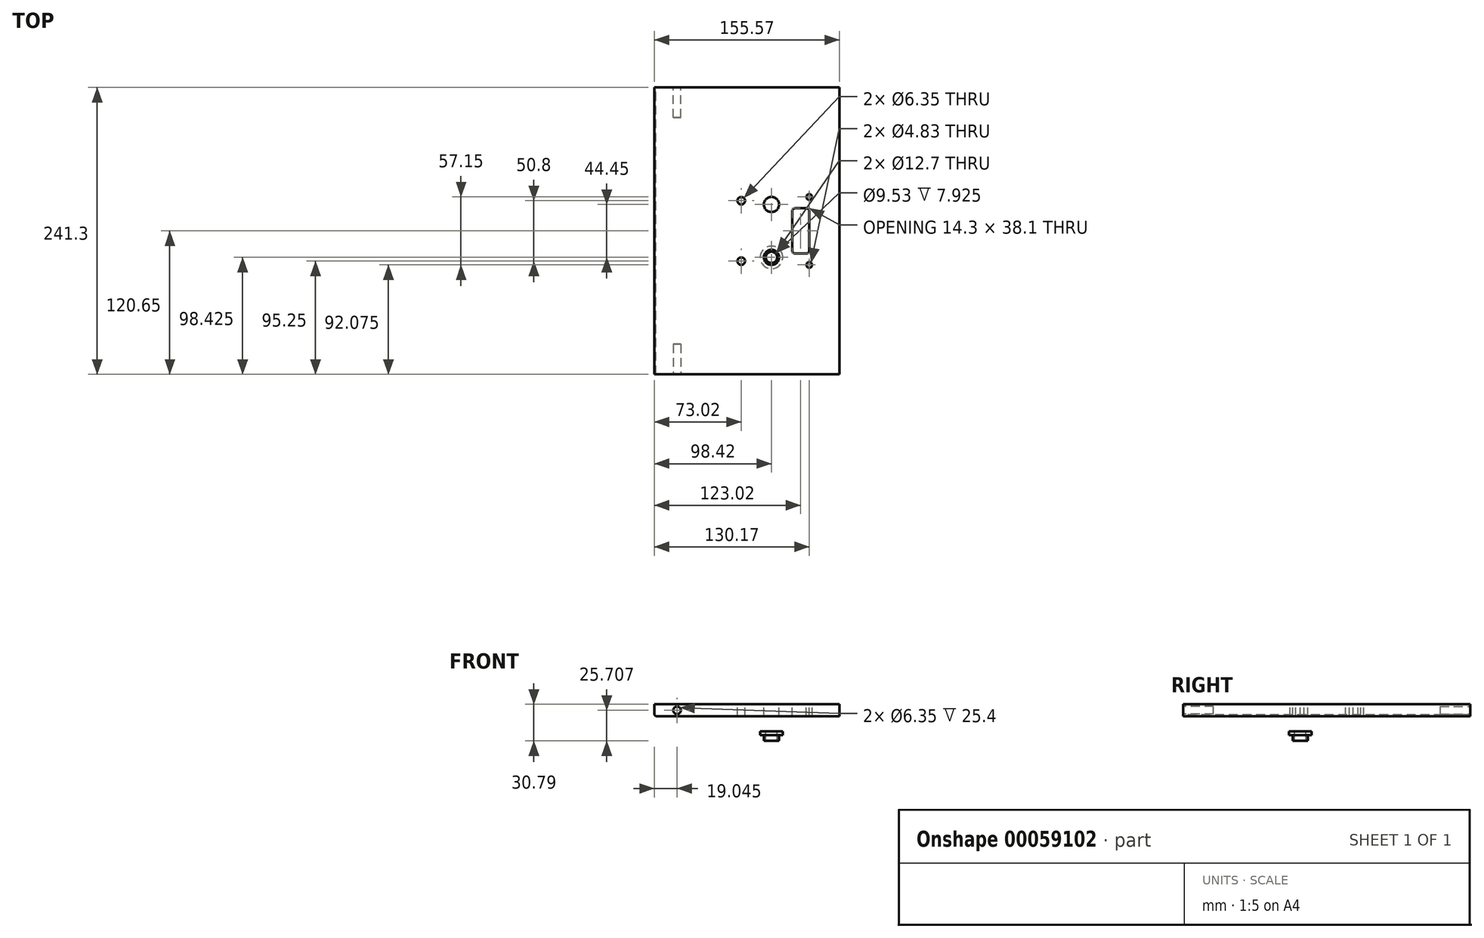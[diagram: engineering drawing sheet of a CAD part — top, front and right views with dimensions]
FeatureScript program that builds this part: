
annotation { "Feature Type Name" : "Feature", "Feature Type Description" : "" }
export const myFeature = defineFeature(function(context is Context, id is Id, definition is map)
    precondition{}
    {
        {
            var Q0;
            Q0=qCreatedBy(makeId("Front.planeOp"),FACE);
            var sketch = newSketch(context, id + "F0", { "sketchPlane" : qUnion([Q0])});
            skLineSegment(sketch, "E0.rect.bottom", {"start": v(50.8, -4.76) * mm, "end": v(-88.9, -4.76) * mm});
            skLineSegment(sketch, "E0.rect.top", {"start": v(50.8, 5.4) * mm, "end": v(-88.9, 5.4) * mm});
            skLineSegment(sketch, "E0.rect.right", {"start": v(-88.9, -4.76) * mm, "end": v(-88.9, 5.4) * mm});
            skPoint(sketch, "E0.rect.middle", {"position": v(0, 0) * mm});
            skLineSegment(sketch, "E1", {"start": v(50.8, 5.4) * mm, "end": v(50.8, -4.76) * mm});
            skSolve(sketch);
        }
        {
            var Q0;
            Q0=makeQuery(id+"F0.imprint","IMPRINT",FACE,{"disambiguationData":[TD([[makeQuery(id+"F0.imprint","IMPRINT",EDGE,{"derivedFrom":sQuery(id+"F0.wireOp",EDGE,"E0.rect.bottom")}),-1.0]])]});
            extrude(context, id + "F1", {"entities" : qUnion([Q0]), "depth" : 120.65 * mm, "hasSecondDirection" : true, "secondDirectionOppositeDirection" : true, "secondDirectionDepth" : 120.65 * mm});
        }
        {
            var Q0;
            Q0=makeQuery(id+"F1.opExtrude","SWEPT_FACE",FACE,{"disambiguationData":[OSD([sQuery(id+"F0.wireOp",EDGE,"E0.rect.top")])]});
            var sketch = newSketch(context, id + "F2", { "sketchPlane" : qUnion([Q0])});
            skLineSegment(sketch, "E2", {"start": v(-19.05, 120.65) * mm, "end": v(-19.05, -120.65) * mm, "construction": true});
            skLineSegment(sketch, "E3", {"start": v(-31.75, 120.65) * mm, "end": v(-31.75, -120.65) * mm, "construction": true});
            skLineSegment(sketch, "E4", {"start": v(-88.9, 25.4) * mm, "end": v(50.8, 25.4) * mm, "construction": true});
            skLineSegment(sketch, "E5", {"start": v(-88.9, -25.4) * mm, "end": v(50.8, -25.4) * mm, "construction": true});
            skCircle(sketch, "E6", {"center": v(-31.75, 25.4) * mm, "radius": 3.18 * mm});
            skCircle(sketch, "E7", {"center": v(-31.75, -25.4) * mm, "radius": 3.18 * mm});
            skLineSegment(sketch, "E8", {"start": v(-6.35, 120.65) * mm, "end": v(-6.35, -120.65) * mm, "construction": true});
            skCircle(sketch, "E9", {"center": v(-6.35, 22.22) * mm, "radius": 6.35 * mm});
            skCircle(sketch, "E10", {"center": v(-6.35, -22.23) * mm, "radius": 6.35 * mm});
            skLineSegment(sketch, "E11", {"start": v(9.52, 120.65) * mm, "end": v(9.53, -120.65) * mm, "construction": true});
            skLineSegment(sketch, "E12", {"start": v(25.4, 120.65) * mm, "end": v(25.4, -120.65) * mm, "construction": true});
            skPoint(sketch, "E13.oppositeSnap0", {"position": v(25.4, 0) * mm});
            skLineSegment(sketch, "E13.left", {"start": v(11.1, 19.05) * mm, "end": v(11.1, -19.05) * mm});
            skLineSegment(sketch, "E13.right", {"start": v(25.4, 19.05) * mm, "end": v(25.4, -19.05) * mm});
            skLineSegment(sketch, "E14", {"start": v(11.1, 19.05) * mm, "end": v(25.4, 19.05) * mm});
            skLineSegment(sketch, "E15", {"start": v(11.1, -19.05) * mm, "end": v(25.4, -19.05) * mm});
            skPoint(sketch, "E16.orphan", {"position": v(25.4, -25.4) * mm});
            skLineSegment(sketch, "E17", {"start": v(9.52, 28.58) * mm, "end": v(25.4, 28.58) * mm, "construction": true});
            skLineSegment(sketch, "E18", {"start": v(9.52, -28.57) * mm, "end": v(25.4, -28.57) * mm, "construction": true});
            skCircle(sketch, "E19", {"center": v(25.4, 28.58) * mm, "radius": 2.41 * mm});
            skCircle(sketch, "E20", {"center": v(25.4, -28.57) * mm, "radius": 2.41 * mm});
            skLineSegment(sketch, "E21", {"start": v(-88.9, 0) * mm, "end": v(50.8, 0) * mm, "construction": true});
            skSolve(sketch);
        }
        {
            var Q0;
            Q0=makeQuery(id+"F2.imprint","IMPRINT",FACE,{"disambiguationData":[TD([[makeQuery(id+"F2.imprint","IMPRINT",EDGE,{"derivedFrom":sQuery(id+"F2.wireOp",EDGE,"E6")}),1.0]])]});
            var Q1;
            Q1=makeQuery(id+"F2.imprint","IMPRINT",FACE,{"disambiguationData":[TD([[makeQuery(id+"F2.imprint","IMPRINT",EDGE,{"derivedFrom":sQuery(id+"F2.wireOp",EDGE,"E7")}),1.0]])]});
            var Q2;
            Q2=makeQuery(id+"F2.imprint","IMPRINT",FACE,{"disambiguationData":[TD([[makeQuery(id+"F2.imprint","IMPRINT",EDGE,{"derivedFrom":sQuery(id+"F2.wireOp",EDGE,"E9")}),1.0]])]});
            var Q3;
            Q3=makeQuery(id+"F2.imprint","IMPRINT",FACE,{"disambiguationData":[TD([[makeQuery(id+"F2.imprint","IMPRINT",EDGE,{"derivedFrom":sQuery(id+"F2.wireOp",EDGE,"E10")}),1.0]])]});
            var Q4;
            Q4=makeQuery(id+"F2.imprint","IMPRINT",FACE,{"disambiguationData":[TD([[makeQuery(id+"F2.imprint","IMPRINT",EDGE,{"derivedFrom":sQuery(id+"F2.wireOp",EDGE,"E19")}),1.0]])]});
            var Q5;
            Q5=makeQuery(id+"F2.imprint","IMPRINT",FACE,{"disambiguationData":[TD([[makeQuery(id+"F2.imprint","IMPRINT",EDGE,{"derivedFrom":sQuery(id+"F2.wireOp",EDGE,"E20")}),1.0]])]});
            var Q6;
            Q6=makeQuery(id+"F2.imprint","IMPRINT",FACE,{"disambiguationData":[TD([[makeQuery(id+"F2.imprint","IMPRINT",EDGE,{"derivedFrom":sQuery(id+"F2.wireOp",EDGE,"E13.left")}),1.0]])]});
            extrude(context, id + "F3", {"entities" : qUnion([Q0, Q1, Q2, Q3, Q4, Q5, Q6]), "operationType" : NewBodyOperationType.REMOVE, "endBound" : BoundingType.THROUGH_ALL, "oppositeDirection" : true, "depth" : 25.4 * mm});
        }
        {
            var Q0;
            Q0=makeQuery(id+"F3.boolean.opBoolean","COPY",EDGE,{"derivedFrom":makeQuery(id+"F3.opExtrude","SWEPT_EDGE",EDGE,{"disambiguationData":[OSD([sQuery(id+"F2.wireOp",EDGE,"E13.left"),sQuery(id+"F2.wireOp",EDGE,"E14")])]})});
            var Q1;
            Q1=makeQuery(id+"F3.boolean.opBoolean","COPY",EDGE,{"derivedFrom":makeQuery(id+"F3.opExtrude","SWEPT_EDGE",EDGE,{"disambiguationData":[OSD([sQuery(id+"F2.wireOp",EDGE,"E13.right"),sQuery(id+"F2.wireOp",EDGE,"E14")])]})});
            var Q2;
            Q2=makeQuery(id+"F3.boolean.opBoolean","COPY",EDGE,{"derivedFrom":makeQuery(id+"F3.opExtrude","SWEPT_EDGE",EDGE,{"disambiguationData":[OSD([sQuery(id+"F2.wireOp",EDGE,"E13.left"),sQuery(id+"F2.wireOp",EDGE,"E15")])]})});
            var Q3;
            Q3=makeQuery(id+"F3.boolean.opBoolean","COPY",EDGE,{"derivedFrom":makeQuery(id+"F3.opExtrude","SWEPT_EDGE",EDGE,{"disambiguationData":[OSD([sQuery(id+"F2.wireOp",EDGE,"E13.right"),sQuery(id+"F2.wireOp",EDGE,"E15")])]})});
            fillet(context, id + "F4", {"entities" : qUnion([Q0, Q1, Q2, Q3]), "radius" : 2.54 * mm, "tangentPropagation" : true, "allowEdgeOverflow" : false});
        }
        {
            var Q0;
            Q0=makeQuery(id+"F1.opExtrude","SWEPT_FACE",FACE,{"disambiguationData":[OSD([sQuery(id+"F0.wireOp",EDGE,"E0.rect.right")])]});
            extrude(context, id + "F5", {"entities" : qUnion([Q0]), "operationType" : NewBodyOperationType.ADD, "depth" : 15.88 * mm});
        }
        {
            var Q0;
            {var subQ0=sQuery(id+"F0.wireOp",EDGE,"E0.rect.right");Q0=makeQuery(id+"F5.boolean.opBoolean","MERGE",FACE,{"derivedFrom":[makeQuery(id+"F1.opExtrude","CAP_FACE",FACE,{"disambiguationData":[OSD([sQuery(id+"F0.wireOp",EDGE,"E0.rect.bottom"),sQuery(id+"F0.wireOp",EDGE,"E0.rect.top"),subQ0,sQuery(id+"F0.wireOp",EDGE,"E1")])],"isStart":false}),makeQuery(id+"F5.opExtrude","SWEPT_FACE",FACE,{"disambiguationData":[OSD([subQ0]),TDD([makeQuery(id+"F1.opExtrude","CAP_EDGE",EDGE,{"disambiguationData":[OSD([subQ0])],"isStart":false})])]})]});}
            var sketch = newSketch(context, id + "F6", { "sketchPlane" : qUnion([Q0])});
            skLineSegment(sketch, "E22", {"start": v(-58.45, 0) * mm, "end": v(-104.77, 0) * mm, "construction": true});
            skLineSegment(sketch, "E23", {"start": v(-85.72, 5.4) * mm, "end": v(-85.72, -4.76) * mm, "construction": true});
            skCircle(sketch, "E24", {"center": v(-85.72, 0.32) * mm, "radius": 3.18 * mm});
            skSolve(sketch);
        }
        {
            var Q0;
            Q0=makeQuery(id+"F6.imprint","IMPRINT",FACE,{"disambiguationData":[TD([[makeQuery(id+"F6.imprint","IMPRINT",EDGE,{"derivedFrom":sQuery(id+"F6.wireOp",EDGE,"E24")}),1.0]])]});
            extrude(context, id + "F7", {"entities" : qUnion([Q0]), "operationType" : NewBodyOperationType.REMOVE, "oppositeDirection" : true, "depth" : 25.4 * mm});
        }
        {
            var Q0;
            {var subQ0=sQuery(id+"F0.wireOp",EDGE,"E0.rect.right");Q0=makeQuery(id+"F5.boolean.opBoolean","MERGE",FACE,{"derivedFrom":[makeQuery(id+"F1.opExtrude","CAP_FACE",FACE,{"disambiguationData":[OSD([sQuery(id+"F0.wireOp",EDGE,"E0.rect.bottom"),sQuery(id+"F0.wireOp",EDGE,"E0.rect.top"),subQ0,sQuery(id+"F0.wireOp",EDGE,"E1")])],"isStart":true}),makeQuery(id+"F5.opExtrude","SWEPT_FACE",FACE,{"disambiguationData":[OSD([subQ0]),TDD([makeQuery(id+"F1.opExtrude","CAP_EDGE",EDGE,{"disambiguationData":[OSD([subQ0])],"isStart":true})])]})]});}
            var sketch = newSketch(context, id + "F8", { "sketchPlane" : qUnion([Q0])});
            skLineSegment(sketch, "E25", {"start": v(63.13, 0) * mm, "end": v(104.77, 0) * mm, "construction": true});
            skLineSegment(sketch, "E26", {"start": v(85.72, 5.4) * mm, "end": v(85.72, -4.76) * mm, "construction": true});
            skCircle(sketch, "E27", {"center": v(85.72, 0.32) * mm, "radius": 3.18 * mm});
            skSolve(sketch);
        }
        {
            var Q0;
            Q0=makeQuery(id+"F8.imprint","IMPRINT",FACE,{"disambiguationData":[TD([[makeQuery(id+"F8.imprint","IMPRINT",EDGE,{"derivedFrom":sQuery(id+"F8.wireOp",EDGE,"E27")}),1.0]])]});
            extrude(context, id + "F9", {"entities" : qUnion([Q0]), "operationType" : NewBodyOperationType.REMOVE, "oppositeDirection" : true, "depth" : 25.4 * mm});
        }
        {
            var Q0;
            Q0=makeQuery(id+"F5.opExtrude","CAP_EDGE",EDGE,{"disambiguationData":[OSD([sQuery(id+"F0.wireOp",EDGE,"E0.rect.bottom"),sQuery(id+"F0.wireOp",EDGE,"E0.rect.right")])],"isStart":false});
            chamfer(context, id + "F10", {"entities" : qUnion([Q0]), "width" : 1.27 * mm, "tangentPropagation" : true});
        }
        {
            var Q0;
            {var subQ0=sQuery(id+"F0.wireOp",EDGE,"E0.rect.bottom");Q0=makeQuery(id+"F5.boolean.opBoolean","MERGE",FACE,{"derivedFrom":[makeQuery(id+"F1.opExtrude","SWEPT_FACE",FACE,{"disambiguationData":[OSD([subQ0])]}),makeQuery(id+"F5.opExtrude","SWEPT_FACE",FACE,{"disambiguationData":[OSD([subQ0,sQuery(id+"F0.wireOp",EDGE,"E0.rect.right")])]})]});}
            cPlane(context, id + "F11", {"entities" : qUnion([Q0]), "cplaneType" : CPlaneType.OFFSET, "offset" : 12.7 * mm, "width" : 152.4 * mm, "height" : 152.4 * mm});
        }
        {
            var Q0;
            Q0=qCreatedBy(id+"F11.planeOp",FACE);
            var sketch = newSketch(context, id + "F12", { "sketchPlane" : qUnion([Q0])});
            skCircle(sketch, "E28.0", {"center": v(-6.35, 22.23) * mm, "radius": 6.35 * mm, "construction": true});
            skCircle(sketch, "E29", {"center": v(-6.35, 22.23) * mm, "radius": 9.53 * mm});
            skCircle(sketch, "E30", {"center": v(-6.35, 22.23) * mm, "radius": 4.76 * mm});
            skSolve(sketch);
        }
        {
            var Q0;
            Q0=makeQuery(id+"F12.imprint","IMPRINT",FACE,{"disambiguationData":[TD([[makeQuery(id+"F12.imprint","IMPRINT",EDGE,{"derivedFrom":sQuery(id+"F12.wireOp",EDGE,"E29")}),1.0]])]});
            extrude(context, id + "F13", {"entities" : qUnion([Q0]), "depth" : 3.17 * mm});
        }
        {
            var Q0;
            Q0=makeQuery(id+"F13.opExtrude","CAP_FACE",FACE,{"disambiguationData":[OSD([sQuery(id+"F12.wireOp",EDGE,"E29"),sQuery(id+"F12.wireOp",EDGE,"E30")])],"isStart":false});
            var sketch = newSketch(context, id + "F14", { "sketchPlane" : qUnion([Q0])});
            skCircle(sketch, "E31.0", {"center": v(-6.35, 22.23) * mm, "radius": 4.76 * mm});
            skCircle(sketch, "E32.0", {"center": v(-6.35, 22.23) * mm, "radius": 6.35 * mm});
            skSolve(sketch);
        }
        {
            var Q0;
            Q0=makeQuery(id+"F14.imprint","IMPRINT",FACE,{"disambiguationData":[TD([[makeQuery(id+"F14.imprint","IMPRINT",EDGE,{"derivedFrom":sQuery(id+"F14.wireOp",EDGE,"E31.0")}),-1.0]])]});
            extrude(context, id + "F15", {"entities" : qUnion([Q0]), "operationType" : NewBodyOperationType.ADD, "depth" : 4.75 * mm});
        }
    });
